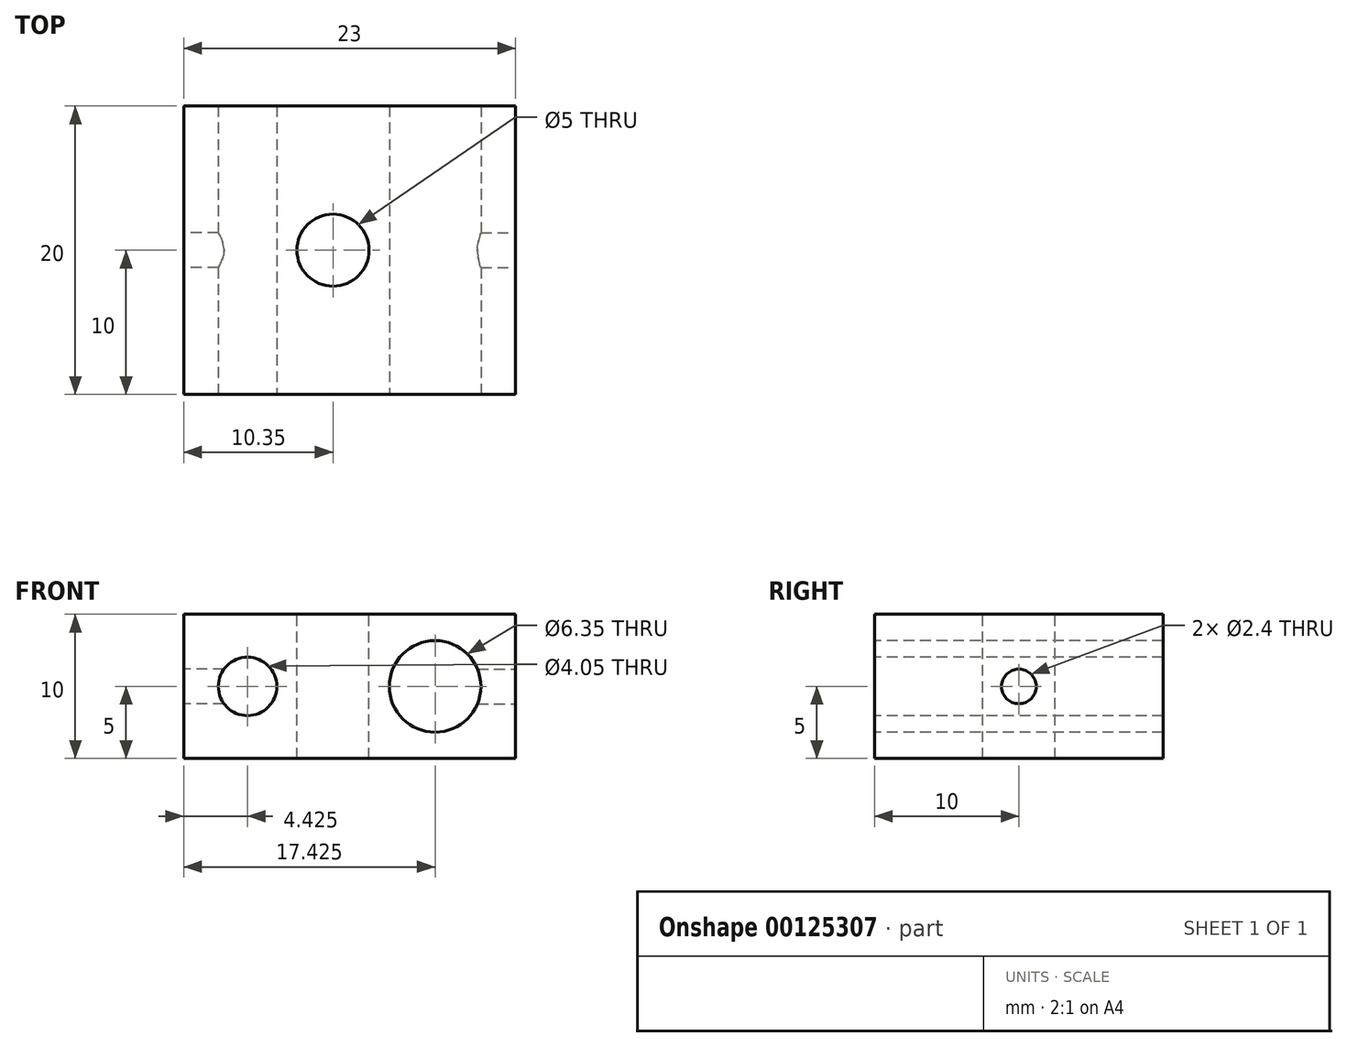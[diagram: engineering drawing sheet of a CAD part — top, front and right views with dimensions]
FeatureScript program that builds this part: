
annotation { "Feature Type Name" : "Feature", "Feature Type Description" : "" }
export const myFeature = defineFeature(function(context is Context, id is Id, definition is map)
    precondition{}
    {
        {
            var Q0;
            Q0=qCreatedBy(makeId("Top.planeOp"),FACE);
            var sketch = newSketch(context, id + "F0", { "sketchPlane" : qUnion([Q0])});
            skLineSegment(sketch, "E0.bottom", {"start": v(11.5, -10) * mm, "end": v(-11.5, -10) * mm});
            skLineSegment(sketch, "E0.top", {"start": v(11.5, 10) * mm, "end": v(-11.5, 10) * mm});
            skLineSegment(sketch, "E0.left", {"start": v(11.5, -10) * mm, "end": v(11.5, 10) * mm});
            skLineSegment(sketch, "E0.right", {"start": v(-11.5, -10) * mm, "end": v(-11.5, 10) * mm});
            skPoint(sketch, "E0.middle", {"position": v(0, 0) * mm});
            skSolve(sketch);
        }
        {
            var Q0;
            Q0 = qSketchRegion(id + "F0", true);
            extrude(context, id + "F1", {"entities" : qUnion([Q0]), "endBound" : BoundingType.SYMMETRIC, "depth" : 10 * mm});
        }
        {
            var Q0;
            Q0=makeQuery(id+"F1.opExtrude","SWEPT_FACE",FACE,{"disambiguationData":[OSD([sQuery(id+"F0.wireOp",EDGE,"E0.bottom")])]});
            var sketch = newSketch(context, id + "F2", { "sketchPlane" : qUnion([Q0])});
            skCircle(sketch, "E1", {"center": v(-7.08, 0) * mm, "radius": 2.02 * mm});
            skCircle(sketch, "E2", {"center": v(5.92, 0) * mm, "radius": 3.17 * mm});
            skLineSegment(sketch, "E3", {"start": v(0, 14.47) * mm, "end": v(0, -13.81) * mm, "construction": true});
            skSolve(sketch);
        }
        {
            var Q0;
            Q0 = qSketchRegion(id + "F2", true);
            extrude(context, id + "F3", {"entities" : qUnion([Q0]), "operationType" : NewBodyOperationType.REMOVE, "oppositeDirection" : true, "depth" : 25 * mm});
        }
        {
            var Q0;
            Q0=makeQuery(id+"F1.opExtrude","CAP_FACE",FACE,{"disambiguationData":[OSD([sQuery(id+"F0.wireOp",EDGE,"E0.bottom"),sQuery(id+"F0.wireOp",EDGE,"E0.top"),sQuery(id+"F0.wireOp",EDGE,"E0.left"),sQuery(id+"F0.wireOp",EDGE,"E0.right")])],"isStart":false});
            var sketch = newSketch(context, id + "F4", { "sketchPlane" : qUnion([Q0])});
            skPoint(sketch, "E4", {"position": v(-1.15, 0) * mm});
            skLineSegment(sketch, "E5.0", {"start": v(-5.05, 10) * mm, "end": v(-9.1, 10) * mm, "construction": true});
            skLineSegment(sketch, "E6.0", {"start": v(9.1, 10) * mm, "end": v(2.75, 10) * mm, "construction": true});
            skLineSegment(sketch, "E7", {"start": v(-5.05, 10) * mm, "end": v(2.75, 10) * mm, "construction": true});
            skLineSegment(sketch, "E8", {"start": v(-1.15, 10) * mm, "end": v(-1.15, -13.75) * mm, "construction": true});
            skSolve(sketch);
        }
        {
            var Q0;
            Q0=sQuery(id+"F4.wireOp",VERTEX,"E4");
            var Q1;
            Q1=makeQuery(id+"F1.opExtrude","SWEPT_BODY",BODY,{"disambiguationData":[OSD([sQuery(id+"F0.wireOp",EDGE,"E0.bottom"),sQuery(id+"F0.wireOp",EDGE,"E0.top"),sQuery(id+"F0.wireOp",EDGE,"E0.left"),sQuery(id+"F0.wireOp",EDGE,"E0.right")])]});
            hole(context, id + "F5", {"style" : HoleStyle.SIMPLE, "endStyle" : HoleEndStyle.THROUGH, "standardTappedOrClearance" : lookupTablePath({ "standard" : "ISO", "engagement" : "75%", "pitch" : "1 mm", "size" : "M6", "type" : "Tapped" }), "standardBlindInLast" : lookupTablePath({ "standard" : "ISO", "engagement" : "75%", "pitch" : "1 mm", "size" : "M6", "type" : "Tapped" }), "holeDiameter" : 5 * mm, "startFromSketch" : true, "locations" : qUnion([Q0]), "scope" : qUnion([Q1]), "isTappedThrough" : true, "majorDiameter" : 6 * mm, "showTappedDepth" : true});
        }
        {
            var Q0;
            Q0=makeQuery(id+"F1.opExtrude","SWEPT_FACE",FACE,{"disambiguationData":[OSD([sQuery(id+"F0.wireOp",EDGE,"E0.right")])]});
            var sketch = newSketch(context, id + "F6", { "sketchPlane" : qUnion([Q0])});
            skPoint(sketch, "E9", {"position": v(0, 0) * mm});
            skSolve(sketch);
        }
        {
            var Q0;
            Q0=sQuery(id+"F6.wireOp",VERTEX,"E9");
            var Q1;
            Q1=makeQuery(id+"F1.opExtrude","SWEPT_BODY",BODY,{"disambiguationData":[OSD([sQuery(id+"F0.wireOp",EDGE,"E0.bottom"),sQuery(id+"F0.wireOp",EDGE,"E0.top"),sQuery(id+"F0.wireOp",EDGE,"E0.left"),sQuery(id+"F0.wireOp",EDGE,"E0.right")])]});
            hole(context, id + "F7", {"style" : HoleStyle.SIMPLE, "endStyle" : HoleEndStyle.BLIND, "standardTappedOrClearance" : lookupTablePath({ "standard" : "ISO", "engagement" : "75%", "pitch" : "0.6 mm", "size" : "M3", "type" : "Tapped" }), "standardBlindInLast" : lookupTablePath({ "standard" : "ISO", "engagement" : "75%", "pitch" : "0.6 mm", "size" : "M3", "type" : "Tapped" }), "holeDiameter" : 2.4 * mm, "holeDepth" : 5 * mm, "startFromSketch" : true, "locations" : qUnion([Q0]), "scope" : qUnion([Q1])});
        }
        {
            var Q0;
            Q0=makeQuery(id+"F1.opExtrude","SWEPT_FACE",FACE,{"disambiguationData":[OSD([sQuery(id+"F0.wireOp",EDGE,"E0.left")])]});
            var sketch = newSketch(context, id + "F8", { "sketchPlane" : qUnion([Q0])});
            skPoint(sketch, "E10", {"position": v(0, 0) * mm});
            skSolve(sketch);
        }
        {
            var Q0;
            Q0=sQuery(id+"F8.wireOp",VERTEX,"E10");
            var Q1;
            Q1=makeQuery(id+"F1.opExtrude","SWEPT_BODY",BODY,{"disambiguationData":[OSD([sQuery(id+"F0.wireOp",EDGE,"E0.bottom"),sQuery(id+"F0.wireOp",EDGE,"E0.top"),sQuery(id+"F0.wireOp",EDGE,"E0.left"),sQuery(id+"F0.wireOp",EDGE,"E0.right")])]});
            hole(context, id + "F9", {"style" : HoleStyle.SIMPLE, "endStyle" : HoleEndStyle.BLIND, "standardTappedOrClearance" : lookupTablePath({ "standard" : "ISO", "engagement" : "75%", "pitch" : "0.6 mm", "size" : "M3", "type" : "Tapped" }), "standardBlindInLast" : lookupTablePath({ "standard" : "ISO", "engagement" : "75%", "pitch" : "0.6 mm", "size" : "M3", "type" : "Tapped" }), "holeDiameter" : 2.4 * mm, "holeDepth" : 5 * mm, "startFromSketch" : true, "locations" : qUnion([Q0]), "scope" : qUnion([Q1])});
        }
    });
